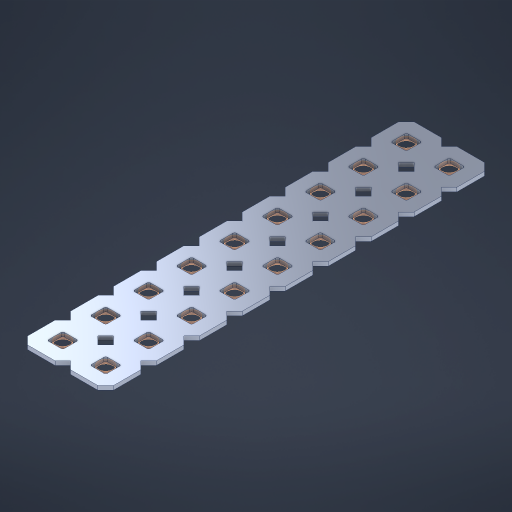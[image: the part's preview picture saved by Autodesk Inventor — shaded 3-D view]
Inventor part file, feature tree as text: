
AUTODESK INVENTOR PART (.ipt)
format: ipt  version: 2023 (Build 270158000, 158)  size: 456,704 bytes
history: native  units: in
note: dims shown in document units (in); Inventor stores cm internally (conversion verified against a paired STEP export)
features: other x19, extrude x17, sketch x2, pattern_linear x1
ambient origin geometry x8: Origin, YZ Plane, XZ Plane, XY Plane, X Axis, Y Axis, Z Axis, Center Point
bodies: Solid1 (feature_tree), Body (feature_tree)
feature tree (39):
  pattern_linear  "Rectangular Pattern1"  Spacing1=0.09in  [1 undecoded]
  sketch  "Sketch1"  dims[d1=0.5in]
  sketch  "Sketch2"  dims[d2=0.182in d3=0.09in d4=0.09in d5=0.09in d6=0.09in d7=0.09in d8=0.09in d9=0.09in d10=0.09in d11=0.02in d13=0.0in d14=0.172in d15=0.0625in d16=0.0in d19=0.5in d22=0.5in]
  other  "Srf1"
  other  "Srf126"
  other  "Srf127"
  other  "Srf128"
  other  "Srf129"
  other  "Srf130"
  other  "Srf131"
  other  "Srf250"
  other  "Srf251"
  other  "Srf268"
  other  "Srf269"
  other  "Srf270"
  other  "Srf271"
  other  "Srf272"
  other  "Srf273"
  other  "Srf274"
  other  "Srf275"
  other  "Srf276"
  other  "Circle"
  extrude  "ExtrusionSrf126"  Depth=0.09in
  extrude  "ExtrusionSrf127"  Depth=0.09in
  extrude  "ExtrusionSrf128"  Depth=0.09in
  extrude  "ExtrusionSrf129"  Depth=0.09in
  extrude  "ExtrusionSrf130"  Depth=0.09in
  extrude  "ExtrusionSrf131"  Depth=0.09in
  extrude  "ExtrusionSrf250"  Depth=0.09in
  extrude  "ExtrusionSrf251"  Depth=0.02in
  extrude  "ExtrusionSrf268"  TaperAngle=0.0deg  [1 undecoded]
  extrude  "ExtrusionSrf269"  Depth=0.5in
  extrude  "ExtrusionSrf270"  Depth=0.5in TaperAngle=0.0deg
  extrude  "ExtrusionSrf271"  Depth=0.5in
  extrude  "ExtrusionSrf272"  Depth=0.5in
  extrude  "ExtrusionSrf273"  [1 undecoded]
  extrude  "ExtrusionSrf274"  [1 undecoded]
  extrude  "ExtrusionSrf275"  [1 undecoded]
  extrude  "ExtrusionSrf276"  [1 undecoded]
note: 6 required parameter values undecoded (feature->parameter linkage not recoverable at this tier; creation-order binding heuristic only, values carry confidence <= 0.55)
